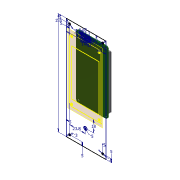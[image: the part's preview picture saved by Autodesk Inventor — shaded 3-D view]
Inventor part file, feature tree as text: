
AUTODESK INVENTOR PART (.ipt)
format: ipt  version: 2016 (Build 200138000, 138)  size: 192,000 bytes
history: native  units: mm
features: sketch x5, projected_geometry x5, extrude x4, plane x1
ambient origin geometry x8: Origin, YZ Plane, XZ Plane, XY Plane, X Axis, Y Axis, Z Axis, Center Point
bodies: Solid1 (feature_tree), Solid2 (feature_tree), Solid3 (feature_tree), Solid4 (feature_tree)
feature tree (15):
  extrude  "Extrusion1"  Depth=95.0mm
  extrude  "Extrusion2"  Depth=3.2mm
  extrude  "Extrusion3"  Depth=3.2mm
  extrude  "Extrusion4"  Depth=1.6mm TaperAngle=0.0deg
  plane  "Work Plane1"
  sketch  "Sketch5"  dims[d9=7.05mm d10=7.05mm d11=2.8mm d12=0.0mm d13=2.0mm d14=1.2mm d15=0.0mm d16=2.92mm d17=69.6mm d18=41.2mm d19=0.0mm d20=0.1mm d21=0.0mm d22=10.0mm d23=155.0mm d24=60.0mm d25=5.0mm d26=3.0mm d27=5.0mm d28=5.0mm d29=3.0mm d30=5.0mm d31=5.0mm d32=3.0mm d33=3.0mm d34=5.0mm d35=5.0mm d36=5.0mm d37=5.0mm d38=5.0mm d39=23.8mm d40=18.0mm d41=14.6mm d42=7.2mm d43=12.5mm d44=5.1mm d45=0.0mm d46=0.0mm d47=0.0mm d48=0.92mm d49=0.92mm d50=0.92mm d51=0.92mm d52=2.0mm d53=2.5mm d54=2.5mm d55=1.0mm d56=2.3mm d57=2.3mm d58=13.3mm d59=6.65mm d60=2.4mm d61=2.4mm d62=1.3mm d63=1.3mm d64=1.3mm d65=1.3mm d66=3.0mm]
  sketch  "Sketch1"  dims[d0=47.6mm d1=95.0mm]
  sketch  "Sketch2"  dims[d2=3.2mm d3=3.2mm]
  projected_geometry  "Projected Loop1"
  sketch  "Sketch3"  dims[d4=3.2mm d5=3.2mm]
  projected_geometry  "Projected Loop2"
  sketch  "Sketch4"  dims[d6=3.2mm d7=1.6mm d8=0.0mm]
  projected_geometry  "Projected Loop3"
  projected_geometry  "Projected Loop4"
  projected_geometry  "Projected Loop5"
